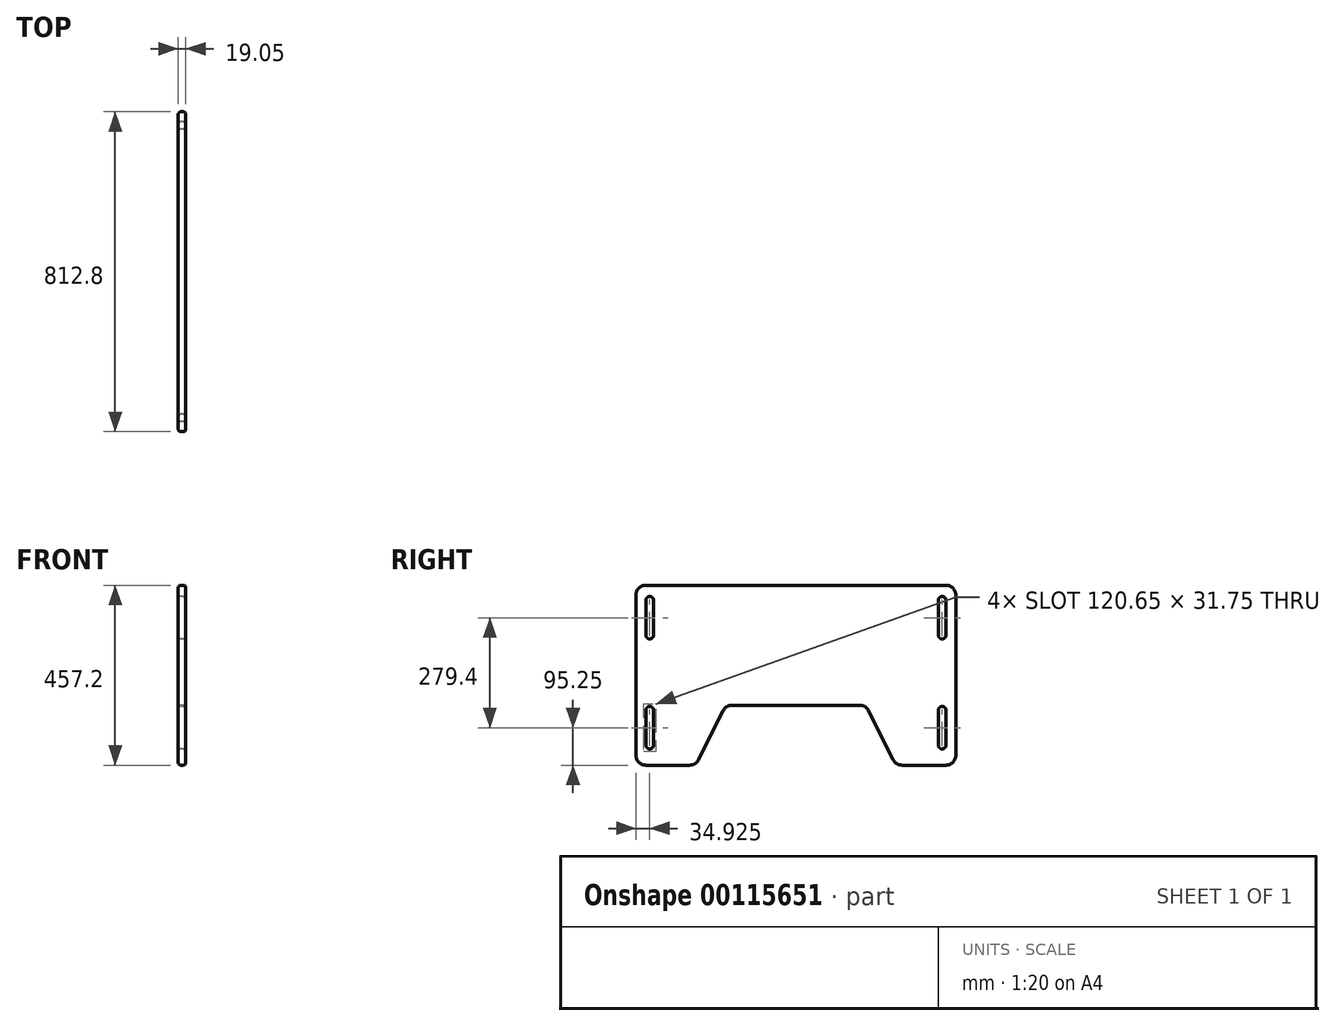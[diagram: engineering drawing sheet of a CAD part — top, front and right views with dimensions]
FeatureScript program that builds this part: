
annotation { "Feature Type Name" : "Feature", "Feature Type Description" : "" }
export const myFeature = defineFeature(function(context is Context, id is Id, definition is map)
    precondition{}
    {
        {
            var Q0;
            Q0=qCreatedBy(makeId("Right.planeOp"),FACE);
            var sketch = newSketch(context, id + "F0", { "sketchPlane" : qUnion([Q0])});
            skLineSegment(sketch, "E0.bottom", {"start": v(-406.4, 457.2) * mm, "end": v(406.4, 457.2) * mm});
            skLineSegment(sketch, "E0.top", {"start": v(-406.4, 0) * mm, "end": v(-254, 0) * mm});
            skLineSegment(sketch, "E0.left", {"start": v(-406.4, 457.2) * mm, "end": v(-406.4, 0) * mm});
            skLineSegment(sketch, "E0.right", {"start": v(406.4, 457.2) * mm, "end": v(406.4, 0) * mm});
            skLineSegment(sketch, "E1", {"start": v(0, 457.2) * mm, "end": v(0, 0) * mm, "construction": true});
            skLineSegment(sketch, "E2", {"start": v(-254, 0) * mm, "end": v(-177.8, 152.4) * mm});
            skLineSegment(sketch, "E3", {"start": v(-177.8, 152.4) * mm, "end": v(177.8, 152.4) * mm});
            skLineSegment(sketch, "E4", {"start": v(177.8, 152.4) * mm, "end": v(254, 0) * mm});
            skLineSegment(sketch, "E5.trimOffspring", {"start": v(254, 0) * mm, "end": v(406.4, 0) * mm});
            skLineSegment(sketch, "E6", {"start": v(-371.48, 419.1) * mm, "end": v(-371.48, 330.2) * mm, "construction": true});
            skArc(sketch, "E7.0.startCap", {"start": v(-381, 419.1) * mm, "mid": v(-371.48, 428.63) * mm, "end": v(-361.95, 419.1) * mm});
            skArc(sketch, "E7.0.endCap", {"start": v(-361.95, 330.2) * mm, "mid": v(-371.48, 320.68) * mm, "end": v(-381, 330.2) * mm});
            skLineSegment(sketch, "E7.0.left", {"start": v(-361.95, 419.1) * mm, "end": v(-361.95, 330.2) * mm});
            skLineSegment(sketch, "E7.0.right", {"start": v(-381, 419.1) * mm, "end": v(-381, 330.2) * mm});
            skLineSegment(sketch, "E8", {"start": v(-371.48, 139.7) * mm, "end": v(-371.48, 50.8) * mm, "construction": true});
            skArc(sketch, "E9.0.startCap", {"start": v(-381, 139.7) * mm, "mid": v(-371.48, 149.22) * mm, "end": v(-361.95, 139.7) * mm});
            skArc(sketch, "E9.0.endCap", {"start": v(-361.95, 50.8) * mm, "mid": v(-371.48, 41.28) * mm, "end": v(-381, 50.8) * mm});
            skLineSegment(sketch, "E9.0.left", {"start": v(-361.95, 139.7) * mm, "end": v(-361.95, 50.8) * mm});
            skLineSegment(sketch, "E9.0.right", {"start": v(-381, 139.7) * mm, "end": v(-381, 50.8) * mm});
            skArc(sketch, "E10.MirrorCS", {"start": v(381, 139.7) * mm, "mid": v(371.48, 149.23) * mm, "end": v(361.95, 139.7) * mm});
            skArc(sketch, "E11.MirrorCS", {"start": v(361.95, 50.8) * mm, "mid": v(371.48, 41.28) * mm, "end": v(381, 50.8) * mm});
            skLineSegment(sketch, "E12.MirrorCS", {"start": v(371.48, 419.1) * mm, "end": v(371.48, 330.2) * mm, "construction": true});
            skLineSegment(sketch, "E13.MirrorCS", {"start": v(371.48, 139.7) * mm, "end": v(371.48, 50.8) * mm, "construction": true});
            skLineSegment(sketch, "E14.MirrorCS", {"start": v(361.95, 419.1) * mm, "end": v(361.95, 330.2) * mm});
            skArc(sketch, "E15.MirrorCS", {"start": v(361.95, 330.2) * mm, "mid": v(371.47, 320.68) * mm, "end": v(381, 330.2) * mm});
            skArc(sketch, "E16.MirrorCS", {"start": v(381, 419.1) * mm, "mid": v(371.48, 428.63) * mm, "end": v(361.95, 419.1) * mm});
            skLineSegment(sketch, "E17.MirrorCS", {"start": v(381, 139.7) * mm, "end": v(381, 50.8) * mm});
            skLineSegment(sketch, "E18.MirrorCS", {"start": v(361.95, 139.7) * mm, "end": v(361.95, 50.8) * mm});
            skLineSegment(sketch, "E19.MirrorCS", {"start": v(381, 419.1) * mm, "end": v(381, 330.2) * mm});
            skSolve(sketch);
        }
        {
            var Q0;
            Q0 = qSketchRegion(id + "F0", true);
            extrude(context, id + "F1", {"entities" : qUnion([Q0]), "depth" : 19.05 * mm});
        }
        {
            var Q0;
            Q0=makeQuery(id+"F1.opExtrude","SWEPT_EDGE",EDGE,{"disambiguationData":[OSD([sQuery(id+"F0.wireOp",EDGE,"E0.bottom"),sQuery(id+"F0.wireOp",EDGE,"E0.left")])]});
            var Q1;
            Q1=makeQuery(id+"F1.opExtrude","SWEPT_EDGE",EDGE,{"disambiguationData":[OSD([sQuery(id+"F0.wireOp",EDGE,"E0.bottom"),sQuery(id+"F0.wireOp",EDGE,"E0.right")])]});
            var Q2;
            Q2=makeQuery(id+"F1.opExtrude","SWEPT_EDGE",EDGE,{"disambiguationData":[OSD([sQuery(id+"F0.wireOp",EDGE,"E0.top"),sQuery(id+"F0.wireOp",EDGE,"E0.left")])]});
            var Q3;
            Q3=makeQuery(id+"F1.opExtrude","SWEPT_EDGE",EDGE,{"disambiguationData":[OSD([sQuery(id+"F0.wireOp",EDGE,"E0.right"),sQuery(id+"F0.wireOp",EDGE,"E5.trimOffspring")])]});
            var Q4;
            Q4=makeQuery(id+"F1.opExtrude","SWEPT_EDGE",EDGE,{"disambiguationData":[OSD([sQuery(id+"F0.wireOp",EDGE,"E2"),sQuery(id+"F0.wireOp",EDGE,"E3")])]});
            var Q5;
            Q5=makeQuery(id+"F1.opExtrude","SWEPT_EDGE",EDGE,{"disambiguationData":[OSD([sQuery(id+"F0.wireOp",EDGE,"E0.top"),sQuery(id+"F0.wireOp",EDGE,"E2")])]});
            var Q6;
            Q6=makeQuery(id+"F1.opExtrude","SWEPT_EDGE",EDGE,{"disambiguationData":[OSD([sQuery(id+"F0.wireOp",EDGE,"E4"),sQuery(id+"F0.wireOp",EDGE,"E5.trimOffspring")])]});
            var Q7;
            Q7=makeQuery(id+"F1.opExtrude","SWEPT_EDGE",EDGE,{"disambiguationData":[OSD([sQuery(id+"F0.wireOp",EDGE,"E3"),sQuery(id+"F0.wireOp",EDGE,"E4")])]});
            fillet(context, id + "F2", {"entities" : qUnion([Q0, Q1, Q2, Q3, Q4, Q5, Q6, Q7]), "radius" : 25.4 * mm, "tangentPropagation" : true, "allowEdgeOverflow" : false});
        }
        {
            var Q0;
            Q0=makeQuery(id+"F1.opExtrude","CAP_EDGE",EDGE,{"disambiguationData":[OSD([sQuery(id+"F0.wireOp",EDGE,"E0.bottom")])],"isStart":false});
            var Q1;
            Q1=makeQuery(id+"F1.opExtrude","CAP_EDGE",EDGE,{"disambiguationData":[OSD([sQuery(id+"F0.wireOp",EDGE,"E0.bottom")])],"isStart":true});
            var Q2;
            Q2=makeQuery(id+"F1.opExtrude","CAP_EDGE",EDGE,{"disambiguationData":[OSD([sQuery(id+"F0.wireOp",EDGE,"E7.0.left")])],"isStart":false});
            var Q3;
            Q3=makeQuery(id+"F1.opExtrude","CAP_EDGE",EDGE,{"disambiguationData":[OSD([sQuery(id+"F0.wireOp",EDGE,"E9.0.left")])],"isStart":false});
            var Q4;
            Q4=makeQuery(id+"F1.opExtrude","CAP_EDGE",EDGE,{"disambiguationData":[OSD([sQuery(id+"F0.wireOp",EDGE,"E17.MirrorCS")])],"isStart":false});
            var Q5;
            Q5=makeQuery(id+"F1.opExtrude","CAP_EDGE",EDGE,{"disambiguationData":[OSD([sQuery(id+"F0.wireOp",EDGE,"E19.MirrorCS")])],"isStart":false});
            var Q6;
            Q6=makeQuery(id+"F1.opExtrude","CAP_EDGE",EDGE,{"disambiguationData":[OSD([sQuery(id+"F0.wireOp",EDGE,"E14.MirrorCS")])],"isStart":true});
            var Q7;
            Q7=makeQuery(id+"F1.opExtrude","CAP_EDGE",EDGE,{"disambiguationData":[OSD([sQuery(id+"F0.wireOp",EDGE,"E7.0.right")])],"isStart":true});
            var Q8;
            Q8=makeQuery(id+"F1.opExtrude","CAP_EDGE",EDGE,{"disambiguationData":[OSD([sQuery(id+"F0.wireOp",EDGE,"E9.0.right")])],"isStart":true});
            var Q9;
            Q9=makeQuery(id+"F1.opExtrude","CAP_EDGE",EDGE,{"disambiguationData":[OSD([sQuery(id+"F0.wireOp",EDGE,"E18.MirrorCS")])],"isStart":true});
            fillet(context, id + "F3", {"entities" : qUnion([Q0, Q1, Q2, Q3, Q4, Q5, Q6, Q7, Q8, Q9]), "radius" : 6.35 * mm, "tangentPropagation" : true, "allowEdgeOverflow" : false});
        }
    });
